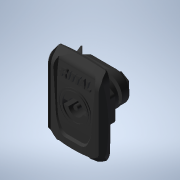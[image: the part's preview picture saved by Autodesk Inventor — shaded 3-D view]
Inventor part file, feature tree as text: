
AUTODESK INVENTOR PART (.ipt)
format: ipt  version: 2021 (Build 250183000, 183)  size: 915,456 bytes
history: native  units: mm
features: sketch x36, extrude x30, other x7, revolve x6, thread x1, pattern_circular x1
ambient origin geometry x8: Origin, YZ Plane, XZ Plane, XY Plane, X Axis, Y Axis, Z Axis, Center Point
bodies: Solid1 (feature_tree)
feature tree (81):
  extrude  "Extrusion1"  Depth=5.7mm
  extrude  "Extrusion2"  Depth=2.0mm TaperAngle=0.0deg
  extrude  "Extrusion3"  Depth=2.0mm TaperAngle=0.0deg
  extrude  "Extrusion4"  Depth=20.0mm TaperAngle=0.0deg
  extrude  "Extrusion5"  Depth=6.981317mm
  extrude  "Extrusion6"  Depth=40.0mm TaperAngle=0.0deg
  extrude  "Extrusion7"  Depth=5.973mm TaperAngle=0.0deg
  extrude  "Extrusion8"  Depth=10.0mm TaperAngle=0.0deg
  extrude  "Extrusion9"  Depth=4.5mm TaperAngle=0.0deg
  revolve  "Revolution1"  [1 undecoded]
  extrude  "Extrusion10"  Depth=13.0mm TaperAngle=0.0deg
  extrude  "Extrusion11"  Depth=3.0mm TaperAngle=0.0deg
  revolve  "Revolution2"  [1 undecoded]
  thread  "Thread1"  [1 undecoded]
  extrude  "Extrusion12"  Depth=1.4mm TaperAngle=0.0deg
  extrude  "Extrusion13"  Depth=7.5mm TaperAngle=0.0deg
  extrude  "Extrusion14"  TaperAngle=360.0deg  [1 undecoded]
  extrude  "Extrusion15"  Depth=4.8mm TaperAngle=0.0deg
  extrude  "Extrusion16"  Depth=60.0mm TaperAngle=60.0deg
  extrude  "Extrusion17"  TaperAngle=0.0deg  [1 undecoded]
  extrude  "Extrusion18"  [1 undecoded]
  extrude  "Extrusion19"  [1 undecoded]
  extrude  "Extrusion20"  [1 undecoded]
  extrude  "Extrusion21"  [1 undecoded]
  extrude  "Extrusion22"  [1 undecoded]
  extrude  "Extrusion23"  [1 undecoded]
  revolve  "Revolution3"  [1 undecoded]
  extrude  "Extrusion24"  [1 undecoded]
  extrude  "Extrusion25"  [1 undecoded]
  extrude  "Extrusion26"  [1 undecoded]
  extrude  "Extrusion27"  [1 undecoded]
  extrude  "Extrusion28"  [1 undecoded]
  revolve  "Revolution4"  [1 undecoded]
  revolve  "Revolution5"  [1 undecoded]
  extrude  "Extrusion29"  [1 undecoded]
  extrude  "Extrusion30"  [1 undecoded]
  pattern_circular  "Circular Pattern1"  [2 undecoded]
  revolve  "Revolution6"  [1 undecoded]
  other  "VV_XY"
  other  "VV_YZ"
  other  "VV_ZX"
  other  "VV_X"
  other  "VV_Y"
  other  "VV_Z"
  other  "VV_Center"
  sketch  "Sketch_6"  dims[d12=32.0mm d13=0.0mm d14=20.0mm d15=0.0mm]
  sketch  "Sketch_1"  dims[d0=55.1mm d1=0.0mm d2=5.7mm d3=-7.330383mm]
  sketch  "Sketch_43"
  sketch  "Sketch_44"
  sketch  "Sketch_46"
  sketch  "Sketch_47"
  sketch  "Sketch_2"  dims[d4=6.0mm d5=0.0mm d6=2.0mm d7=0.0mm]
  sketch  "Sketch_5"  dims[d8=2.0mm d9=0.0mm d10=2.0mm d11=0.0mm]
  sketch  "Sketch_7"  dims[d16=20.0mm d17=0.0mm d18=6.981317mm]
  sketch  "Sketch_8"  dims[d19=43.0mm d20=0.0mm d21=40.0mm d22=0.0mm]
  sketch  "Sketch_9"  dims[d23=360.0deg d24=5.973mm d25=0.0mm]
  sketch  "Sketch_11"  dims[d30=2.4mm d31=0.0mm d32=4.5mm d33=0.0mm]
  sketch  "Sketch_17"  dims[d51=6.0mm d52=0.0mm d53=1.4mm d54=0.0mm]
  sketch  "Sketch_19"  dims[d59=5.0mm d60=0.0mm d61=360.0deg]
  sketch  "Sketch_20"  dims[d62=360.0deg d63=4.8mm d64=0.0mm]
  sketch  "Sketch_18"  dims[d55=6.0mm d56=0.0mm d57=7.5mm d58=0.0mm]
  sketch  "Sketch_21"  dims[d65=0.6mm d66=0.0mm d67=60.0mm d68=60.0deg]
  sketch  "Sketch_22"  dims[d70=360.0deg d71=0.0mm]
  sketch  "Sketch_23"
  sketch  "Sketch_45"
  sketch  "Sketch_24"
  sketch  "Sketch_25"
  sketch  "Sketch_26"
  sketch  "Sketch_27"
  sketch  "Sketch_28"
  sketch  "Sketch_36"
  sketch  "Sketch_10"  dims[d26=10.0mm d27=0.0mm d28=1.07mm d29=0.0mm]
  sketch  "Sketch_12"  dims[d34=2.3mm d35=0.0mm d36=20.0mm d37=0.0mm]
  sketch  "Sketch_16"  dims[d46=3.0mm d47=0.0mm d48=8.0mm d49=0.0mm d50=360.0deg]
  sketch  "Sketch_13"  dims[d38=13.7mm d39=0.0mm d40=13.0mm d41=0.0mm]
  sketch  "Sketch_14"  dims[d42=5.0mm d43=0.0mm d44=3.0mm d45=0.0mm]
  sketch  "Sketch_35"
  sketch  "Sketch_40"
  sketch  "Sketch_41"
  sketch  "Sketch_29"
  sketch  "Sketch_37"
note: 24 required parameter values undecoded (feature->parameter linkage not recoverable at this tier; creation-order binding heuristic only, values carry confidence <= 0.55)